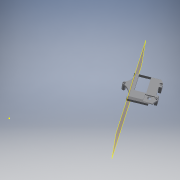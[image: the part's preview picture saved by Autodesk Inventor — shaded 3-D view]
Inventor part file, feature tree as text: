
AUTODESK INVENTOR PART (.ipt)
format: ipt  version: 2016 (Build 200138000, 138)  size: 3,670,016 bytes
history: native  units: in
note: dims shown in document units (in); Inventor stores cm internally (conversion verified against a paired STEP export)
features: extrude x50, sketch x45, fillet x31, projected_geometry x27, other x12, chamfer x9, plane x8, hole x3, mirror x2, shell x1
ambient origin geometry x8: Origin, YZ Plane, XZ Plane, XY Plane, X Axis, Y Axis, Z Axis, Center Point
bodies: Body1 (feature_tree), Body2 (feature_tree), Body3 (feature_tree), Body4 (feature_tree), Body5 (feature_tree), Body6 (feature_tree), Body7 (feature_tree), Body8 (feature_tree)
feature tree (188):
  other  "deck_ehlerscutter.ipt"
  plane  "Work Plane1"
  extrude  "Extrusion1"  Depth=0.3937in
  fillet  "Fillet1"  Radius=0.481in
  extrude  "Extrusion2"  Depth=13.7795in
  extrude  "Extrusion3"  Depth=0.125in
  chamfer  "Chamfer2"  Distance=0.125in
  extrude  "Extrusion5"  Depth=5.5118in
  chamfer  "Chamfer5"  Distance=0.125in Angle=45.0deg
  fillet  "Fillet8"  Radius=0.315in
  fillet  "Fillet9"  Radius=11.0in
  fillet  "Fillet10"  Radius=1.1811in
  fillet  "Fillet11"  Radius=0.7874in
  chamfer  "Chamfer6"  Distance=0.3937in Angle=45.0deg
  fillet  "Fillet12"  Radius=1.9685in
  chamfer  "Chamfer7"  Distance=0.3937in Angle=45.0deg
  fillet  "Fillet13"  Radius=1.5748in
  plane  "Work Plane2"
  shell  "Shell1"  Thickness=0.2756in
  extrude  "Extrusion9"  Depth=5.6299in
  sketch  "Sketch8"  dims[d13=0.7874in]
  extrude  "Extrusion8"  Depth=0.8986in
  extrude  "Extrusion10"  Depth=1.378in
  sketch  "Sketch12"  dims[d40=0.3937in d41=0.125in d42=45.0deg d43=1.1811in d44=0.7874in]
  plane  "Work Plane3"
  extrude  "Extrusion61"  Depth=0.8986in
  extrude  "Extrusion62"  Depth=0.8986in
  plane  "Work Plane4"
  extrude  "Extrusion12"  Depth=0.5512in
  fillet  "Fillet14"  Radius=0.5118in
  fillet  "Fillet15"  [1 undecoded]
  chamfer  "Chamfer8"  Distance=1.1811in
  plane  "Work Plane5"
  extrude  "Extrusion13"  Depth=0.125in
  plane  "Work Plane6"
  extrude  "Extrusion14"  [1 undecoded]
  other  "part_placement_sketch"
  extrude  "Extrusion16"  Depth=0.0787in TaperAngle=0.0deg
  extrude  "Extrusion18"  Depth=0.1969in
  extrude  "Extrusion19"  Depth=0.4134in
  extrude  "Extrusion20"  Depth=0.0591in
  chamfer  "Chamfer9"  Distance=1.1811in
  fillet  "Fillet16"  Radius=1.378in
  fillet  "Fillet20"  Radius=2.0472in
  extrude  "Extrusion22"  Depth=2.0472in
  fillet  "Fillet30"  Radius=2.2047in
  hole  "Hole1"  [1 undecoded]
  extrude  "Extrusion17"  Depth=0.0787in TaperAngle=0.0deg
  extrude  "Extrusion25"  Depth=0.4724in
  plane  "Work Plane10"
  extrude  "Extrusion28"  Depth=0.3543in
  extrude  "Extrusion42"  Depth=0.1378in
  hole  "Hole2"  [1 undecoded]
  hole  "Hole3"  [1 undecoded]
  extrude  "Extrusion30"  Depth=0.1476in
  extrude  "Extrusion32"  Depth=0.748in
  extrude  "Extrusion33"  Depth=0.0787in
  extrude  "Extrusion34"  Depth=0.4724in
  extrude  "Extrusion35"  Depth=0.2362in
  extrude  "Extrusion37"  Depth=0.5512in
  extrude  "Extrusion38"  Depth=0.1575in TaperAngle=0.0deg
  extrude  "Extrusion40"  Depth=0.1181in
  extrude  "Extrusion43"  Depth=0.1181in
  extrude  "Extrusion44"  Depth=0.25in
  fillet  "Fillet24"  Radius=0.0394in
  fillet  "Fillet25"  Radius=0.0625in
  fillet  "Fillet26"  Radius=0.375in
  fillet  "Fillet27"  Radius=0.25in
  fillet  "Fillet28"  Radius=0.1299in
  fillet  "Fillet29"  Radius=0.1299in
  fillet  "Fillet23"  Radius=0.1299in
  extrude  "Extrusion41"  Depth=0.1181in
  extrude  "Extrusion45"  Depth=0.1181in
  extrude  "Extrusion46"  Depth=0.125in
  chamfer  "Chamfer10"  Distance=0.5906in
  plane  "Work Plane11"
  sketch  "Sketch46"  dims[d133=0.4528in d134=0.3543in]
  extrude  "Extrusion48"  Depth=0.3937in
  extrude  "Extrusion49"  Depth=0.125in
  extrude  "Extrusion50"  Depth=0.125in
  extrude  "Extrusion52"  Depth=0.125in TaperAngle=0.0deg
  extrude  "Extrusion53"  Depth=0.125in
  fillet  "Fillet31"  Radius=0.38in
  extrude  "Extrusion54"  Depth=0.125in
  extrude  "Extrusion55"  Depth=0.3937in
  fillet  "Fillet32"  Radius=0.3937in
  fillet  "Fillet33"  Radius=0.1575in
  extrude  "Extrusion56"  Depth=0.125in
  extrude  "Extrusion57"  Depth=0.125in
  extrude  "Extrusion58"  Depth=0.125in
  fillet  "Fillet36"  Radius=0.9843in
  extrude  "Extrusion60"  Depth=0.125in
  fillet  "Fillet42"  Radius=0.5in
  fillet  "Fillet43"  Radius=0.201in
  fillet  "Fillet44"  Radius=0.9843in
  fillet  "Fillet45"  Radius=0.4724in
  fillet  "Fillet46"  Radius=0.3937in
  extrude  "Extrusion63"  Depth=0.1575in
  fillet  "Fillet47"  Radius=0.315in
  fillet  "Fillet48"  Radius=2.0in
  fillet  "Fillet49"  Radius=0.2953in
  extrude  "Extrusion64"  Depth=0.0787in TaperAngle=0.0deg
  mirror  "Mirror1"
  extrude  "Extrusion65"  Depth=0.125in
  mirror  "Mirror2"
  sketch  "Sketch63"  dims[d173=0.1181in d174=0.1181in]
  extrude  "Extrusion66"  Depth=0.125in
  extrude  "Extrusion67"  Depth=0.125in TaperAngle=0.0deg
  chamfer  "Chamfer11"  Distance=0.2244in
  chamfer  "Chamfer12"  Distance=0.2244in
  other  "Solid1::deck_ehlerscutter.ipt"
  other  "TaggingFeature1"
  sketch  "Sketch1"  dims[d0=0.3937in d1=0.7874in d2=0.481in]
  projected_geometry  "Projected Loop1"
  other  "sink"
  sketch  "Sketch2"  dims[d3=0.481in d4=13.7795in]
  projected_geometry  "Projected Loop2"
  other  "curve"
  sketch  "Sketch3"  dims[d5=0.125in d6=0.0in d7=0.7874in d9=0.125in d10=0.0in]
  projected_geometry  "Projected Loop3"
  other  "print"
  sketch  "Sketch5"  dims[d11=4.0in d12=5.5118in]
  sketch  "Sketch9"  dims[d15=0.0in]
  sketch  "Sketch10"  dims[d22=1.378in d23=0.125in d24=45.0deg d25=0.315in d26=11.0in d27=0.0in]
  projected_geometry  "Projected Loop6"
  sketch  "Sketch13"  dims[d45=11.811in]
  sketch  "Sketch14"  dims[d46=1.1811in d47=0.3937in d48=0.125in d49=45.0deg d50=1.9685in d51=0.3937in d52=0.125in d53=45.0deg d54=1.5748in d60=0.2756in]
  sketch  "Sketch17"  dims[d65=3.9764in d66=5.6299in]
  other  "esc_clamp"
  sketch  "Sketch18"  dims[d67=0.8986in d68=0.0in d69=0.2756in]
  projected_geometry  "Projected Loop9"
  projected_geometry  "Projected Loop10"
  sketch  "Sketch19"  dims[d70=1.8898in d71=1.378in]
  projected_geometry  "Projected Loop11"
  sketch  "Sketch21"  dims[d72=0.8986in d73=0.0in d74=11.0in]
  projected_geometry  "Projected Loop12"
  projected_geometry  "Projected Loop13"
  projected_geometry  "Projected Loop14"
  sketch  "Sketch22"  dims[d75=0.8986in d76=0.0in d88=1.0in]
  sketch  "Sketch25"  dims[d89=0.5512in d90=0.5512in d91=0.5118in d92=-1.0236in]
  projected_geometry  "Projected Loop17"
  sketch  "Sketch29"  dims[d93=-1.0236in d94=1.1811in d95=0.0in]
  sketch  "Sketch31"  dims[d96=0.125in d98=0.0625in]
  sketch  "Sketch32"  dims[d99=0.25in d100=0.125in d101=45.0deg d102=-0.0787in]
  sketch  "Sketch33"  dims[d103=0.0787in d104=1.1811in d105=0.0in]
  projected_geometry  "Projected Loop19"
  sketch  "Sketch34"  dims[d106=-0.0787in d107=0.1969in]
  projected_geometry  "Projected Loop20"
  sketch  "Sketch36"  dims[d108=2.126in d109=0.4134in]
  sketch  "Sketch37"  dims[d110=2.2441in d111=0.0591in d112=1.1811in d113=0.0in d116=1.378in d117=2.0472in]
  projected_geometry  "Projected Loop22"
  sketch  "Sketch39"  dims[d118=1.378in d119=2.0472in d120=2.2047in]
  sketch  "Sketch40"  dims[d121=2.5591in d123=0.2756in]
  projected_geometry  "Projected Loop23"
  projected_geometry  "Projected Loop24"
  projected_geometry  "Projected Loop25"
  projected_geometry  "Projected Loop26"
  projected_geometry  "Projected Loop27"
  projected_geometry  "Projected Loop28"
  sketch  "Sketch41"  dims[d124=0.0787in d125=0.8071in d126=0.0in]
  sketch  "Sketch42"  dims[d127=0.4724in d128=0.4724in]
  projected_geometry  "Projected Loop29"
  sketch  "Sketch43"  dims[d129=0.3543in d130=0.3543in]
  other  "led_thing"
  sketch  "Sketch44"  dims[d131=1.75in d132=0.1378in]
  projected_geometry  "Projected Loop30"
  sketch  "Sketch47"  dims[d135=0.1378in d136=0.1476in]
  sketch  "Sketch49"  dims[d137=0.1476in d138=0.1476in]
  projected_geometry  "Projected Loop31"
  sketch  "Sketch50"  dims[d139=0.1476in d140=0.748in]
  projected_geometry  "Projected Loop32"
  sketch  "Sketch51"  dims[d141=0.502in d142=0.0787in]
  sketch  "Sketch52"  dims[d144=1.0in d145=0.0in d146=0.4724in]
  sketch  "Sketch53"  dims[d147=0.0394in d148=0.2362in]
  sketch  "Sketch54"  dims[d149=0.315in d150=0.5512in]
  sketch  "Sketch55"  dims[d151=0.502in d152=0.0in d153=0.1575in d154=0.0in]
  other  "heatsinkriser"
  sketch  "Sketch57"  dims[d155=1.75in d156=0.1181in]
  other  "battery"
  sketch  "Sketch60"  dims[d157=1.75in d158=0.1181in]
  sketch  "Sketch61"  dims[d159=0.0394in d160=0.0625in d161=0.0394in d162=0.0625in d163=0.375in d164=0.0in d167=0.25in d168=0.1299in d169=0.1299in d170=0.1299in]
  sketch  "Sketch62"  dims[d171=0.1181in d172=0.1181in]
  projected_geometry  "Projected Loop35"
  sketch  "Sketch64"  dims[d175=0.3543in d176=0.0in]
  projected_geometry  "Projected Loop36"
  sketch  "Sketch65"  dims[d177=0.126in d178=0.75in d179=0.375in d180=0.25in d181=0.5635in d182=1.0in d183=0.8108in d199=0.0295in d200=0.5906in d201=0.3937in d202=0.3543in d203=0.4134in d204=0.1772in d205=0.0in d214=0.38in d217=0.38in d218=0.1875in d220=1.1811in d222=4.375in d223=0.3937in d225=1.0in d227=0.3937in d228=0.0in d231=0.21in d232=0.75in d233=0.375in d234=0.25in d235=0.5635in d236=1.0in d237=0.8108in d238=0.159in d239=0.75in d240=0.375in d241=0.25in d242=0.5635in d243=1.0in d244=0.8108in d245=0.1575in d246=0.125in d247=45.0deg d248=1.0in d249=0.38in d250=2.625in d251=0.9843in d252=0.0in d253=0.5in d254=0.5in d257=0.201in d258=0.9843in d259=0.0in d260=0.4724in d261=0.3937in d262=0.1575in d263=0.315in d264=2.0in d265=0.0in d267=0.2953in d268=0.0787in d269=0.0in d270=0.9646in d271=1.752in d274=0.2362in d275=0.0in d280=0.2244in d281=0.2244in d282=0.2244in d283=0.0945in d284=0.0in d285=0.315in d286=0.9843in d287=1.0in d288=0.0in d291=1.375in d292=0.3065in d296=1.063in d297=0.0in d298=0.7874in d299=2.2244in d300=0.3937in d301=0.3937in d302=0.9449in d303=0.0in d304=0.3937in d305=0.0in d306=0.1181in d307=0.4079in d308=0.9449in d309=0.0in d310=0.1181in d311=0.2362in d312=0.0in d313=0.0in d314=0.3937in d315=0.1181in d316=0.1969in d317=0.1181in d318=0.1969in d319=0.1969in d320=0.0394in d324=0.9449in d325=0.0in d329=0.0295in d330=0.0in d334=0.0197in d335=0.125in d336=45.0deg d337=45.0deg d338=45.0deg d339=1.0in d340=0.0in d341=1.0in d342=0.0in d343=0.2362in d344=0.8071in d345=1.0in d346=0.0in d351=0.2362in d352=0.3937in d353=1.0in d354=0.0in d355=0.2165in d356=0.1181in d357=1.0in d358=0.0in d359=0.1181in d360=0.1969in d361=0.2362in d362=0.0in d363=0.1772in d364=0.1181in d365=0.0in d366=0.0787in d367=0.0787in d369=0.0787in d370=0.0in d371=2.2in d372=3.05in d373=0.0787in d374=0.0in d376=2.2in d377=3.05in d378=0.125in d379=0.0in d381=0.0625in d415=1.5748in d416=1.5748in d417=0.0984in d418=0.6299in d419=0.6299in d420=1.5748in d422=360.0deg d424=0.0787in d425=1.5748in d427=0.1575in d428=1.5748in d430=0.1575in d433=0.125in d434=0.0in d435=1.1811in d436=0.0394in d437=0.125in d438=0.8986in d439=0.0in d440=0.0in d441=0.125in d442=0.0in d443=4.0in d444=10.0in d445=0.125in d446=1.0in d447=0.0in d448=0.0394in d449=0.0625in d450=0.25in d451=0.201in d452=0.375in d453=0.75in d454=3.937in d456=0.875in d457=0.3937in d459=1.0in d461=1.0in d462=0.0in d463=0.1616in d464=3.937in d466=0.875in d467=0.3937in d469=1.0in d471=0.125in d472=0.0in d473=0.7677in d474=0.8071in d475=0.0787in d476=0.0in d477=0.0394in d478=0.1181in d479=0.2362in d480=0.4331in d481=0.2165in d482=0.0787in d483=0.0in d484=0.0197in d485=0.125in d486=45.0deg d487=0.0787in d488=0.125in d489=45.0deg]
  projected_geometry  "Projected Loop37"
  other  "wood"
note: 5 required parameter values undecoded (feature->parameter linkage not recoverable at this tier; creation-order binding heuristic only, values carry confidence <= 0.55)
